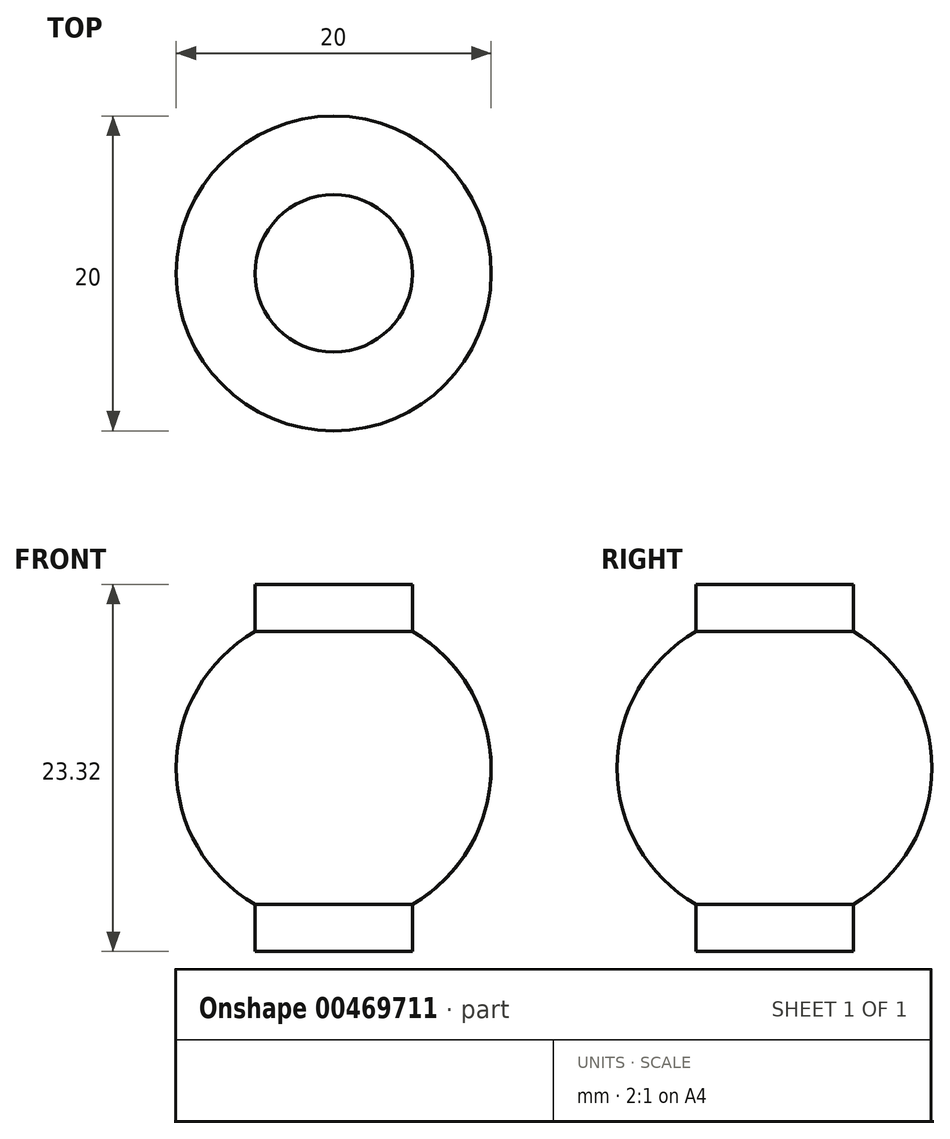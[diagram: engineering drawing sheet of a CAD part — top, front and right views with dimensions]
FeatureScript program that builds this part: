
annotation { "Feature Type Name" : "Feature", "Feature Type Description" : "" }
export const myFeature = defineFeature(function(context is Context, id is Id, definition is map)
    precondition{}
    {
        {
            var Q0;
            Q0=qCreatedBy(makeId("Front.planeOp"),FACE);
            var sketch = newSketch(context, id + "F0", { "sketchPlane" : qUnion([Q0])});
            skArc(sketch, "E0", {"start": v(0, 10) * mm, "mid": v(-10, 0) * mm, "end": v(0, -10) * mm});
            skLineSegment(sketch, "E1", {"start": v(-5, 11.66) * mm, "end": v(0, 11.66) * mm});
            skLineSegment(sketch, "E2", {"start": v(-5, 11.66) * mm, "end": v(-5, 8.66) * mm});
            skLineSegment(sketch, "E3.MirrorCS", {"start": v(-5, -11.66) * mm, "end": v(0, -11.66) * mm});
            skLineSegment(sketch, "E4.MirrorCS", {"start": v(-5, -11.66) * mm, "end": v(-5, -8.66) * mm});
            skLineSegment(sketch, "E5", {"start": v(0, 14.11) * mm, "end": v(0, -13.67) * mm});
            skSolve(sketch);
        }
        {
            var Q0;
            {var subQ0=sQuery(id+"F0.wireOp",EDGE,"E5");var subQ1=sQuery(id+"F0.wireOp",EDGE,"E0");var subQ2=makeQuery(id+"F0.imprint","INTERSECT",VERTEX,{"disambiguationData":[OD(0.0)],"derivedFrom":[subQ1,subQ0]});Q0=makeQuery(id+"F0.imprint","IMPRINT",FACE,{"disambiguationData":[TD([[makeQuery(id+"F0.imprint","IMPRINT",EDGE,{"disambiguationData":[TD([[subQ2,-1.0]])],"derivedFrom":subQ1}),1.0]])]});}
            var Q1;
            {var subQ4=sQuery(id+"F0.wireOp",EDGE,"E1");Q1=makeQuery(id+"F0.imprint","IMPRINT",FACE,{"disambiguationData":[TD([[makeQuery(id+"F0.imprint","IMPRINT",EDGE,{"derivedFrom":subQ4}),-1.0]])]});}
            var Q2;
            {var subQ4=sQuery(id+"F0.wireOp",EDGE,"E3.MirrorCS");Q2=makeQuery(id+"F0.imprint","IMPRINT",FACE,{"disambiguationData":[TD([[makeQuery(id+"F0.imprint","IMPRINT",EDGE,{"derivedFrom":subQ4}),1.0]])]});}
            var Q3;
            Q3=sQuery(id+"F0.wireOp",EDGE,"E5");
            revolve(context, id + "F1", {"entities" : qUnion([Q0, Q1, Q2]), "axis" : qUnion([Q3]), "revolveType" : RevolveType.FULL});
        }
    });
